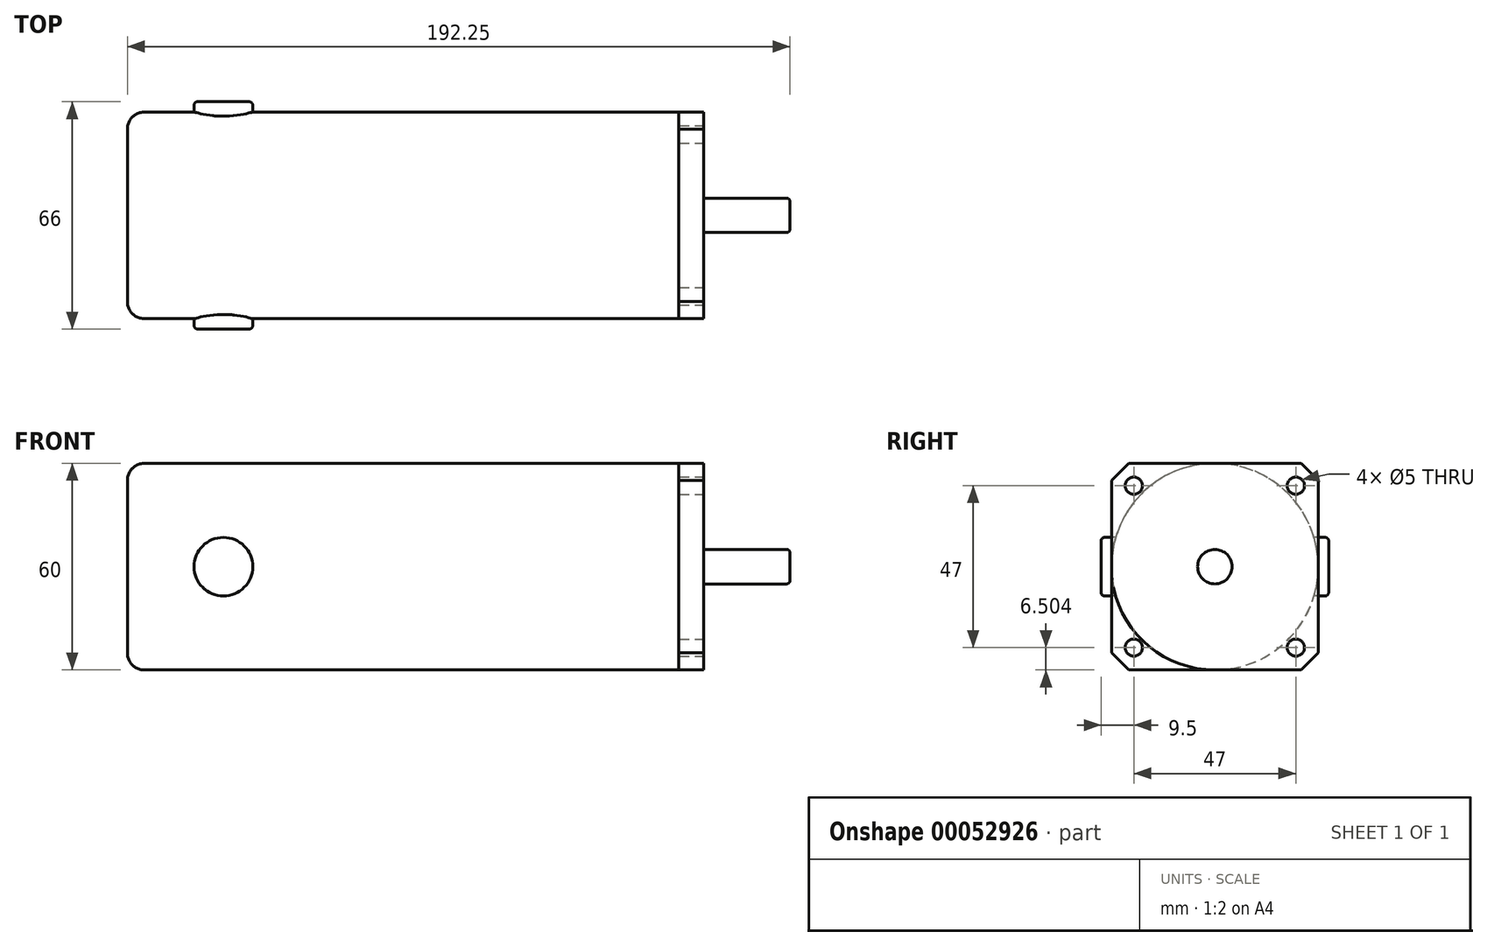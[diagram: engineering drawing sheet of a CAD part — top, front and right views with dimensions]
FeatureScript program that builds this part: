
annotation { "Feature Type Name" : "Feature", "Feature Type Description" : "" }
export const myFeature = defineFeature(function(context is Context, id is Id, definition is map)
    precondition{}
    {
        {
            var Q0;
            Q0=qCreatedBy(makeId("Front.planeOp"),FACE);
            var sketch = newSketch(context, id + "F0", { "sketchPlane" : qUnion([Q0])});
            skLineSegment(sketch, "E0", {"start": v(-42.76, 13.6) * mm, "end": v(157.17, 13.6) * mm, "construction": true});
            skLineSegment(sketch, "E1", {"start": v(157.17, 13.6) * mm, "end": v(157.17, 18.6) * mm});
            skLineSegment(sketch, "E2", {"start": v(157.17, 18.6) * mm, "end": v(132.17, 18.6) * mm});
            skLineSegment(sketch, "E3", {"start": v(132.17, 18.6) * mm, "end": v(132.17, 43.6) * mm});
            skLineSegment(sketch, "E4", {"start": v(132.17, 43.6) * mm, "end": v(-35.08, 43.6) * mm});
            skLineSegment(sketch, "E5", {"start": v(-35.08, 43.6) * mm, "end": v(-35.08, 13.6) * mm});
            skLineSegment(sketch, "E6", {"start": v(-35.08, 13.6) * mm, "end": v(157.17, 13.6) * mm});
            skSolve(sketch);
        }
        {
            var Q0;
            Q0=makeQuery(id+"F0.imprint","IMPRINT",FACE,{"disambiguationData":[TD([[makeQuery(id+"F0.imprint","IMPRINT",EDGE,{"derivedFrom":sQuery(id+"F0.wireOp",EDGE,"E1")}),1.0]])]});
            var Q1;
            Q1=sQuery(id+"F0.wireOp",EDGE,"E0");
            revolve(context, id + "F1", {"entities" : qUnion([Q0]), "axis" : qUnion([Q1]), "revolveType" : RevolveType.FULL});
        }
        {
            var Q0;
            Q0=makeQuery(id+"F1.opRevolve","SWEPT_FACE",FACE,{"disambiguationData":[OSD([sQuery(id+"F0.wireOp",EDGE,"E3")])]});
            var sketch = newSketch(context, id + "F2", { "sketchPlane" : qUnion([Q0])});
            skLineSegment(sketch, "E7.bottom", {"start": v(-30, 43.6) * mm, "end": v(30, 43.6) * mm});
            skLineSegment(sketch, "E7.top", {"start": v(-30, -16.4) * mm, "end": v(30, -16.4) * mm});
            skLineSegment(sketch, "E7.left", {"start": v(-30, 43.6) * mm, "end": v(-30, -16.4) * mm});
            skLineSegment(sketch, "E7.right", {"start": v(30, 43.6) * mm, "end": v(30, -16.4) * mm});
            skSolve(sketch);
        }
        {
            var Q0;
            Q0=qSketchRegion(id+"F2",true);
            extrude(context, id + "F3", {"entities" : qUnion([Q0]), "operationType" : NewBodyOperationType.ADD, "oppositeDirection" : true, "depth" : 7.25 * mm});
        }
        {
            var Q0;
            Q0=makeQuery(id+"F3.boolean.opBoolean","MERGE",FACE,{"derivedFrom":[makeQuery(id+"F1.opRevolve","SWEPT_FACE",FACE,{"disambiguationData":[OSD([sQuery(id+"F0.wireOp",EDGE,"E3")])]}),makeQuery(id+"F3.opExtrude","CAP_FACE",FACE,{"disambiguationData":[OSD([sQuery(id+"F2.wireOp",EDGE,"E7.bottom"),sQuery(id+"F2.wireOp",EDGE,"E7.top"),sQuery(id+"F2.wireOp",EDGE,"E7.left"),sQuery(id+"F2.wireOp",EDGE,"E7.right")])],"isStart":true})]});
            var sketch = newSketch(context, id + "F4", { "sketchPlane" : qUnion([Q0])});
            skLineSegment(sketch, "E8.bottom", {"start": v(-23.5, 37.1) * mm, "end": v(23.5, 37.1) * mm});
            skLineSegment(sketch, "E8.top", {"start": v(-23.5, -9.9) * mm, "end": v(23.5, -9.9) * mm});
            skLineSegment(sketch, "E8.left", {"start": v(-23.5, 37.1) * mm, "end": v(-23.5, -9.9) * mm});
            skLineSegment(sketch, "E8.right", {"start": v(23.5, 37.1) * mm, "end": v(23.5, -9.9) * mm});
            skPoint(sketch, "E9", {"position": v(0, 37.1) * mm});
            skPoint(sketch, "E10", {"position": v(0, 43.6) * mm});
            skPoint(sketch, "E11", {"position": v(-23.5, 13.6) * mm});
            skPoint(sketch, "E12", {"position": v(-30, 13.6) * mm});
            skSolve(sketch);
        }
        {
            var Q0;
            Q0=sQuery(id+"F4.wireOp",VERTEX,"E8.left.start");
            var Q1;
            Q1=sQuery(id+"F4.wireOp",VERTEX,"E8.right.start");
            var Q2;
            Q2=sQuery(id+"F4.wireOp",VERTEX,"E8.left.end");
            var Q3;
            Q3=sQuery(id+"F4.wireOp",VERTEX,"E8.top.end");
            var Q4;
            Q4=makeQuery(id+"F1.opRevolve","SWEPT_BODY",BODY,{"disambiguationData":[OSD([sQuery(id+"F0.wireOp",EDGE,"E1"),sQuery(id+"F0.wireOp",EDGE,"E2"),sQuery(id+"F0.wireOp",EDGE,"E3"),sQuery(id+"F0.wireOp",EDGE,"E4"),sQuery(id+"F0.wireOp",EDGE,"E5"),sQuery(id+"F0.wireOp",EDGE,"E6")])]});
            hole(context, id + "F5", {"style" : HoleStyle.SIMPLE, "holeDiameter" : 5 * mm, "endStyle" : HoleEndStyle.THROUGH, "locations" : qUnion([Q0, Q1, Q2, Q3]), "scope" : qUnion([Q4])});
        }
        {
            var Q0;
            Q0=makeQuery(id+"F3.opExtrude","SWEPT_EDGE",EDGE,{"disambiguationData":[OSD([sQuery(id+"F2.wireOp",EDGE,"E7.bottom"),sQuery(id+"F2.wireOp",EDGE,"E7.right")])]});
            var Q1;
            Q1=makeQuery(id+"F3.opExtrude","SWEPT_EDGE",EDGE,{"disambiguationData":[OSD([sQuery(id+"F2.wireOp",EDGE,"E7.top"),sQuery(id+"F2.wireOp",EDGE,"E7.right")])]});
            var Q2;
            Q2=makeQuery(id+"F3.opExtrude","SWEPT_EDGE",EDGE,{"disambiguationData":[OSD([sQuery(id+"F2.wireOp",EDGE,"E7.bottom"),sQuery(id+"F2.wireOp",EDGE,"E7.left")])]});
            var Q3;
            Q3=makeQuery(id+"F3.opExtrude","SWEPT_EDGE",EDGE,{"disambiguationData":[OSD([sQuery(id+"F2.wireOp",EDGE,"E7.top"),sQuery(id+"F2.wireOp",EDGE,"E7.left")])]});
            chamfer(context, id + "F6", {"entities" : qUnion([Q0, Q1, Q2, Q3]), "width" : 5 * mm, "tangentPropagation" : true});
        }
        {
            var Q0;
            Q0=makeQuery(id+"F1.opRevolve","SWEPT_EDGE",EDGE,{"disambiguationData":[OSD([sQuery(id+"F0.wireOp",EDGE,"E4"),sQuery(id+"F0.wireOp",EDGE,"E5")])]});
            fillet(context, id + "F7", {"entities" : qUnion([Q0]), "radius" : 5 * mm, "tangentPropagation" : true, "allowEdgeOverflow" : false});
        }
        {
            var Q0;
            Q0=makeQuery(id+"F1.opRevolve","SWEPT_FACE",FACE,{"disambiguationData":[OSD([sQuery(id+"F0.wireOp",EDGE,"E1")])]});
            fillet(context, id + "F8", {"entities" : qUnion([Q0]), "radius" : 1 * mm, "tangentPropagation" : true, "allowEdgeOverflow" : false});
        }
        {
            var Q0;
            Q0=makeQuery(id+"F3.opExtrude","SWEPT_FACE",FACE,{"disambiguationData":[OSD([sQuery(id+"F2.wireOp",EDGE,"E7.right")])]});
            cPlane(context, id + "F9", {"entities" : qUnion([Q0]), "cplaneType" : CPlaneType.OFFSET, "offset" : 30 * mm, "oppositeDirection" : true, "width" : 150 * mm, "height" : 150 * mm});
        }
        {
            var Q0;
            Q0=qCreatedBy(id+"F9.planeOp",FACE);
            var sketch = newSketch(context, id + "F10", { "sketchPlane" : qUnion([Q0])});
            skLineSegment(sketch, "E13.0", {"start": v(30.08, -16.4) * mm, "end": v(30.08, 43.6) * mm, "construction": true});
            skPoint(sketch, "E14", {"position": v(7.2, 13.6) * mm});
            skPoint(sketch, "E14.positionSnap0", {"position": v(30.08, 13.6) * mm});
            skCircle(sketch, "E15", {"center": v(7.2, 13.6) * mm, "radius": 8.5 * mm});
            skSolve(sketch);
        }
        {
            var Q0;
            Q0 = qSketchRegion(id + "F10", true);
            extrude(context, id + "F11", {"entities" : qUnion([Q0]), "operationType" : NewBodyOperationType.ADD, "endBound" : BoundingType.SYMMETRIC, "depth" : 66 * mm});
        }
        {
            var Q0;
            Q0=makeQuery(id+"F11.opExtrude","CAP_EDGE",EDGE,{"disambiguationData":[OSD([sQuery(id+"F10.wireOp",EDGE,"E15")])],"isStart":true});
            var Q1;
            Q1=makeQuery(id+"F11.opExtrude","CAP_EDGE",EDGE,{"disambiguationData":[OSD([sQuery(id+"F10.wireOp",EDGE,"E15")])],"isStart":false});
            fillet(context, id + "F12", {"entities" : qUnion([Q0, Q1]), "radius" : 1 * mm, "tangentPropagation" : true, "allowEdgeOverflow" : false});
        }
    });
